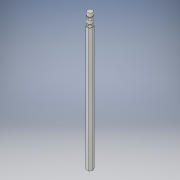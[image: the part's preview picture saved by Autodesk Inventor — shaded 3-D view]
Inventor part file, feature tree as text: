
AUTODESK INVENTOR PART (.ipt)
format: ipt  version: 2017 (Build 210142000, 142)  size: 180,736 bytes
history: native  units: in
note: dims shown in document units (in); Inventor stores cm internally (conversion verified against a paired STEP export)
features: sketch x4, extrude x2, other x2
ambient origin geometry x8: Origin, YZ Plane, XZ Plane, XY Plane, X Axis, Y Axis, Z Axis, Center Point
bodies: Solid1 (feature_tree), Solid2 (feature_tree)
feature tree (8):
  extrude  "wooden part of pencil"  Depth=0.5578in TaperAngle=0.0deg
  extrude  "pencil graphite"  Depth=0.0122in
  other  "connection for pencil and eraser"
  other  "eraser"
  sketch  "Sketch1"  dims[d0=0.023in d1=0.5578in d2=0.0in]
  sketch  "Sketch3"  dims[d3=0.0122in d4=0.0047in]
  sketch  "Sketch4"  dims[d10=0.0019in]
  sketch  "Sketch5"  dims[d13=0.0027in d14=0.0167in d15=0.0045in d16=0.0019in d17=0.0028in d18=0.0014in d20=0.0013in d21=0.0005in d22=0.0027in d23=0.0027in d24=0.0027in d25=0.0027in d26=0.0027in d27=0.0019in d28=0.0018in d29=0.0019in d30=90.0deg d31=0.011in d32=0.0154in d33=90.0deg d34=0.006in d35=0.006in d36=1.0in d37=0.0in]
